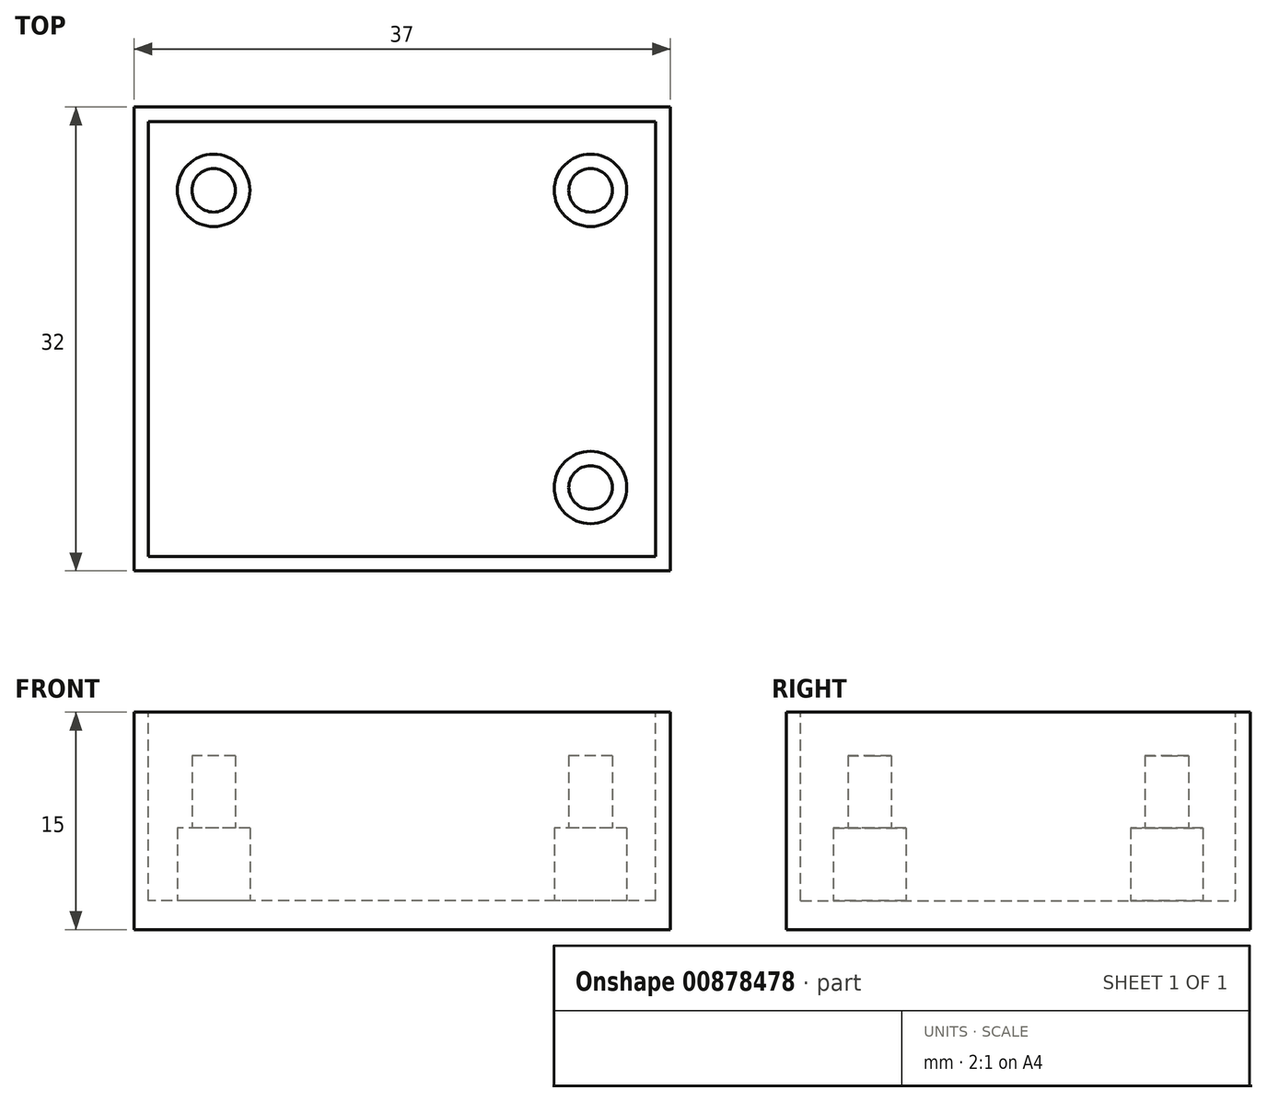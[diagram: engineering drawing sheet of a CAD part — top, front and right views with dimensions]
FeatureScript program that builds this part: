
annotation { "Feature Type Name" : "Feature", "Feature Type Description" : "" }
export const myFeature = defineFeature(function(context is Context, id is Id, definition is map)
    precondition{}
    {
        {
            assignVariable(context, id + "F0", {"name" : "OutsideDepth", "anyValue" : 15});
        }
        {
            var Q0;
            Q0=qCreatedBy(makeId("Top.planeOp"),FACE);
            var sketch = newSketch(context, id + "F1", { "sketchPlane" : qUnion([Q0])});
            skLineSegment(sketch, "E0.bottom", {"start": v(18.5, -16) * mm, "end": v(-18.5, -16) * mm});
            skLineSegment(sketch, "E0.top", {"start": v(18.5, 16) * mm, "end": v(-18.5, 16) * mm});
            skLineSegment(sketch, "E0.left", {"start": v(18.5, -16) * mm, "end": v(18.5, 16) * mm});
            skLineSegment(sketch, "E0.right", {"start": v(-18.5, -16) * mm, "end": v(-18.5, 16) * mm});
            skPoint(sketch, "E0.middle", {"position": v(0, 0) * mm});
            skSolve(sketch);
        }
        {
            var Q0;
            Q0=makeQuery(id+"F1.imprint","IMPRINT",FACE,{"disambiguationData":[TD([[makeQuery(id+"F1.imprint","IMPRINT",EDGE,{"derivedFrom":sQuery(id+"F1.wireOp",EDGE,"E0.bottom")}),-1.0]])]});
            extrude(context, id + "F2", {"entities" : qUnion([Q0]), "depth" : (getVariable(context, 'OutsideDepth')) * mm, "offsetDistance" : 25 * mm});
        }
        {
            var Q0;
            Q0=makeQuery(id+"F2.opExtrude","CAP_FACE",FACE,{"disambiguationData":[OSD([sQuery(id+"F1.wireOp",EDGE,"E0.bottom"),sQuery(id+"F1.wireOp",EDGE,"E0.top"),sQuery(id+"F1.wireOp",EDGE,"E0.left"),sQuery(id+"F1.wireOp",EDGE,"E0.right")])],"isStart":false});
            var sketch = newSketch(context, id + "F3", { "sketchPlane" : qUnion([Q0])});
            skLineSegment(sketch, "E1.bottom", {"start": v(17.5, -15) * mm, "end": v(-17.5, -15) * mm});
            skLineSegment(sketch, "E1.top", {"start": v(17.5, 15) * mm, "end": v(-17.5, 15) * mm});
            skLineSegment(sketch, "E1.left", {"start": v(17.5, -15) * mm, "end": v(17.5, 15) * mm});
            skLineSegment(sketch, "E1.right", {"start": v(-17.5, -15) * mm, "end": v(-17.5, 15) * mm});
            skPoint(sketch, "E1.middle", {"position": v(0, 0) * mm});
            skSolve(sketch);
        }
        {
            var Q0;
            Q0=makeQuery(id+"F3.imprint","IMPRINT",FACE,{"disambiguationData":[TD([[makeQuery(id+"F3.imprint","IMPRINT",EDGE,{"derivedFrom":sQuery(id+"F3.wireOp",EDGE,"E1.bottom")}),-1.0]])]});
            extrude(context, id + "F4", {"entities" : qUnion([Q0]), "operationType" : NewBodyOperationType.REMOVE, "oppositeDirection" : true, "depth" : (getVariable(context, 'OutsideDepth') - 2) * mm, "offsetDistance" : 25 * mm});
        }
        {
            var Q0;
            Q0=makeQuery(id+"F4.boolean.opBoolean","COPY",FACE,{"derivedFrom":makeQuery(id+"F4.opExtrude","CAP_FACE",FACE,{"disambiguationData":[OSD([sQuery(id+"F3.wireOp",EDGE,"E1.bottom"),sQuery(id+"F3.wireOp",EDGE,"E1.top"),sQuery(id+"F3.wireOp",EDGE,"E1.left"),sQuery(id+"F3.wireOp",EDGE,"E1.right")])],"isStart":false})});
            var sketch = newSketch(context, id + "F5", { "sketchPlane" : qUnion([Q0])});
            skLineSegment(sketch, "E2.bottom", {"start": v(13, -10.25) * mm, "end": v(-13, -10.25) * mm, "construction": true});
            skLineSegment(sketch, "E2.top", {"start": v(13, 10.25) * mm, "end": v(-13, 10.25) * mm, "construction": true});
            skLineSegment(sketch, "E2.left", {"start": v(13, -10.25) * mm, "end": v(13, 10.25) * mm, "construction": true});
            skLineSegment(sketch, "E2.right", {"start": v(-13, -10.25) * mm, "end": v(-13, 10.25) * mm, "construction": true});
            skPoint(sketch, "E2.middle", {"position": v(0, 0) * mm});
            skCircle(sketch, "E3", {"center": v(-13, 10.25) * mm, "radius": 2.5 * mm});
            skCircle(sketch, "E4", {"center": v(13, 10.25) * mm, "radius": 2.5 * mm});
            skCircle(sketch, "E5", {"center": v(13, -10.25) * mm, "radius": 2.5 * mm});
            skCircle(sketch, "E6", {"center": v(-13, 10.25) * mm, "radius": 1.5 * mm});
            skCircle(sketch, "E7", {"center": v(13, 10.25) * mm, "radius": 1.5 * mm});
            skCircle(sketch, "E8", {"center": v(13, -10.25) * mm, "radius": 1.5 * mm});
            skSolve(sketch);
        }
        {
            var Q0;
            Q0=makeQuery(id+"F5.imprint","IMPRINT",FACE,{"disambiguationData":[TD([[makeQuery(id+"F5.imprint","IMPRINT",EDGE,{"derivedFrom":sQuery(id+"F5.wireOp",EDGE,"E6")}),1.0]])]});
            var Q1;
            Q1=makeQuery(id+"F5.imprint","IMPRINT",FACE,{"disambiguationData":[TD([[makeQuery(id+"F5.imprint","IMPRINT",EDGE,{"derivedFrom":sQuery(id+"F5.wireOp",EDGE,"E3")}),1.0]])]});
            var Q2;
            Q2=makeQuery(id+"F5.imprint","IMPRINT",FACE,{"disambiguationData":[TD([[makeQuery(id+"F5.imprint","IMPRINT",EDGE,{"derivedFrom":sQuery(id+"F5.wireOp",EDGE,"E7")}),1.0]])]});
            var Q3;
            Q3=makeQuery(id+"F5.imprint","IMPRINT",FACE,{"disambiguationData":[TD([[makeQuery(id+"F5.imprint","IMPRINT",EDGE,{"derivedFrom":sQuery(id+"F5.wireOp",EDGE,"E4")}),1.0]])]});
            var Q4;
            Q4=makeQuery(id+"F5.imprint","IMPRINT",FACE,{"disambiguationData":[TD([[makeQuery(id+"F5.imprint","IMPRINT",EDGE,{"derivedFrom":sQuery(id+"F5.wireOp",EDGE,"E8")}),1.0]])]});
            var Q5;
            Q5=makeQuery(id+"F5.imprint","IMPRINT",FACE,{"disambiguationData":[TD([[makeQuery(id+"F5.imprint","IMPRINT",EDGE,{"derivedFrom":sQuery(id+"F5.wireOp",EDGE,"E5")}),1.0]])]});
            extrude(context, id + "F6", {"entities" : qUnion([Q0, Q1, Q2, Q3, Q4, Q5]), "operationType" : NewBodyOperationType.ADD, "depth" : 5 * mm, "offsetDistance" : 25 * mm});
        }
        {
            var Q0;
            Q0=makeQuery(id+"F5.imprint","IMPRINT",FACE,{"disambiguationData":[TD([[makeQuery(id+"F5.imprint","IMPRINT",EDGE,{"derivedFrom":sQuery(id+"F5.wireOp",EDGE,"E6")}),1.0]])]});
            var Q1;
            Q1=makeQuery(id+"F5.imprint","IMPRINT",FACE,{"disambiguationData":[TD([[makeQuery(id+"F5.imprint","IMPRINT",EDGE,{"derivedFrom":sQuery(id+"F5.wireOp",EDGE,"E7")}),1.0]])]});
            var Q2;
            Q2=makeQuery(id+"F5.imprint","IMPRINT",FACE,{"disambiguationData":[TD([[makeQuery(id+"F5.imprint","IMPRINT",EDGE,{"derivedFrom":sQuery(id+"F5.wireOp",EDGE,"E8")}),1.0]])]});
            extrude(context, id + "F7", {"entities" : qUnion([Q0, Q1, Q2]), "operationType" : NewBodyOperationType.ADD, "depth" : 10 * mm, "offsetDistance" : 25 * mm});
        }
    });
